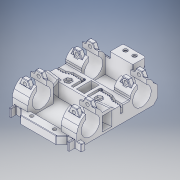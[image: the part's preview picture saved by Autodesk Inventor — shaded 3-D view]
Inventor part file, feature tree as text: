
AUTODESK INVENTOR PART (.ipt)
format: ipt  version: 2019.4 (Build 234330000, 330)  size: 2,265,088 bytes
history: native  units: mm
features: other x88, extrude x37, fillet x12, mirror x8, sketch x8, loft x5, projected_geometry x2, hole x1
ambient origin geometry x8: Origin, YZ Plane, XZ Plane, XY Plane, X Axis, Y Axis, Z Axis, Center Point
bodies: Solid1 (feature_tree)
feature tree (161):
  extrude  "Base"  Depth=67.2mm
  other  "Right Outside Vertical Plane"
  extrude  "Lower Right Rod Holder"  Depth=4.9mm
  fillet  "Bottom Round Fillet"  Radius=1.715mm
  other  "Bottom Rod Clasp Plane"
  other  "Bottom Rod Bottom Screw Hole Plane"
  other  "Bottom Clasp Hole Sketch"
  loft  "Bottom Right Clasp Loft"
  extrude  "Bottom Clasp Hole"  Depth=49.274mm
  other  "Bottom Right Clasp Mirror Plane"
  mirror  "Bottom Right Top Clasp"
  mirror  "Bottom Left Rod Assembly"
  other  "Bottom Middle Extrusion Plane"
  extrude  "Bottom Middle Extrusion"  Depth=4.2mm
  extrude  "Bottom Side Extrusions"  Depth=14.573499mm
  extrude  "Top Rod Extrusion"  Depth=30.281463mm
  other  "Bottom Right Inner Clasp Plane"
  other  "Bottom Left Inner Clasp Plane"
  extrude  "Top Rod Cutout"  Depth=10.0mm TaperAngle=0.0deg
  other  "Top Right Bottom Rod Clasp Plane"
  other  "Top Right Bottom Rod Clasp sketch"
  other  "Bottom Nut Plane"
  other  "Nut Holder Sketch"
  other  "Nut Hole"
  loft  "Bottom Top Right Clasp Loft"
  extrude  "Bottom Top Right Clasp Hole"  Depth=10.0mm
  other  "Top Right Clasp Mirror Plane"
  mirror  "Top Top Right Clasp Assembly"
  mirror  "Top Left Clasp Assembly"
  extrude  "Middle Extrusion"  Depth=10.0mm
  extrude  "Middle Extrusion Center Cutout"  Depth=10.0mm TaperAngle=0.0deg
  other  "Top GT2 Cable Plane"
  extrude  "GT2 Cable Cutout"  Depth=10.0mm
  extrude  "Nut Cutout"  Depth=10.0mm
  other  "Nut Screw Cutout Plane"
  extrude  "Nut Screw Cutout"  TaperAngle=0.0deg  [1 undecoded]
  other  "Right Outside Drag / Cable Plane"
  extrude  "Track Platform"  [1 undecoded]
  extrude  "Sensor Container"  TaperAngle=0.0deg  [1 undecoded]
  extrude  "Insert Holes Cutout"  Depth=10.0mm
  extrude  "Lower Rod Support Extrusion"  Depth=10.0mm TaperAngle=0.0deg
  other  "Right Outside Vertical Plane 2"
  other  "Outside Triangle Bottom Clasp Support Sketch"
  other  "Inside Bottom Clasp Support Plane"
  loft  "Lower Rod Support Loft"
  fillet  "GT2 Bottom Round Fillet (4)"  [1 undecoded]
  mirror  "Lower Rod Support Mirrored"
  fillet  "Bottom Trim Fillets (.2)"  Radius=4.76mm
  fillet  "Bottom Trim Fillets (1)"  Radius=4.76mm
  other  "First Top Track Cut Plane"
  extrude  "First Top Track Cut"  Depth=10.0mm
  extrude  "First Inner Bottom Track Cut Extrusion"  Depth=10.0mm
  other  "First Inner Bottom Angled Track Cut Plane"
  extrude  "First Outer Bottom Track Cut Extrusion"  Depth=10.0mm
  other  "Second Inner Bottom Plane"
  other  "Third Inner Bottom Plane"
  other  "Fourth Inner Bottom Plane"
  other  "Fifth Inner Bottom Plane"
  other  "Sixth Inner Bottom Plane"
  other  "Seventh Inner Bottom Plane"
  other  "First Inner Bottom Angle Plane"
  other  "Second Inner Bottom Angle Plane"
  other  "Third Inner Bottom Angle Plane"
  other  "Fourth Inner Bottom Angle Plane"
  other  "Fifth Inner Bottom Angle Plane"
  other  "Sixth Inner Bottom Angle Plane"
  other  "Eight Inner Bottom Plane"
  other  "Ninth Inner Bottom Plane"
  other  "Tenth Inner Bottom Plane"
  other  "Eleventh Inner Bottom Plane"
  other  "Twelth Inner Bottom Plane"
  other  "Thirteenth Inner Bottom Plane"
  other  "Fourteenth Inner Bottom Plane"
  extrude  "Second Outer Bottom Extrusion"  Depth=10.0mm
  extrude  "Third Outer Bottom Extrusion"  Depth=10.0mm TaperAngle=0.0deg
  extrude  "Fourth Outer Bottom Extrusion"  [1 undecoded]
  other  "Inbetween Fourth Angle Plane"
  extrude  "First Inner Bottom Angle Extrusion"  [1 undecoded]
  other  "First Top Angle Plane"
  other  "First Bend Upper Angle Sketch"
  other  "Second Top Angle Plane"
  extrude  "Top Angle Extrusion"  Depth=10.0mm
  other  "Top Outside Border Plane"
  other  "Top Outside Border Sketch"
  other  "Top Second Insider Border Plane"
  other  "Top Inside Border Sketch"
  other  "Top Insider Border Plane"
  other  "Top Second Insider Border Sketch"
  loft  "Top Inside Border Loft"
  other  "Inside Top Last Border Sketch"
  extrude  "First Bottom Outer Angled Extrusion"  TaperAngle=0.0deg  [1 undecoded]
  extrude  "Second Bottom Outer Angled Extrusion"  [1 undecoded]
  extrude  "Third Bottom Outer Angled Extrusion"  Depth=10.0mm
  extrude  "Fifth Bottom Outer Extrusion"  TaperAngle=0.0deg  [1 undecoded]
  extrude  "Sixth Bottom Outer Extrusion"  TaperAngle=0.0deg  [1 undecoded]
  extrude  "Seventh Bottom Outer Extrusion"  Depth=10.0mm TaperAngle=0.0deg
  extrude  "Eigth Bottom Outer Extrusion"  Depth=10.0mm
  other  "Second Inner Bottom Sketch"
  extrude  "Second Inner Bottom Track Cut Extrusion"  Depth=10.0mm
  loft  "Second Inner Bottom Track Loft"
  mirror  "Track Mirror"
  other  "Right Outside Vertical Plane 3"
  extrude  "Endstop Extrusion (4)"  Depth=10.0mm
  extrude  "Drag / Cable Extrusion (4.6)"  Depth=10.0mm TaperAngle=0.0deg
  hole  "Drag / Cable Holes"  [1 undecoded]
  other  "Vertical Middle Mirror Plane"
  other  "Left Nut Buttom Plane"
  other  "Left Nut Buttom Sketch"
  fillet  "Bottom Middle Trim Fillet (.4)"  Radius=13.0mm
  fillet  "Bottom Top Clasp Fillet (.8)"  Radius=2.2mm
  fillet  "Top Drag / Cable Fillet (1.6)"  Radius=7.85mm
  fillet  "Bottom Drag / Cable Fillet (.4)"  [1 undecoded]
  fillet  "Bottom  Top Wire Holder Fillet (1)"  Radius=6.4mm
  fillet  "Top Top Wire Holder Trim (.3)"  Radius=13.4mm
  fillet  "Top Round Fillet (2.4)"  Radius=1.86mm
  fillet  "Nut Trim Fillets (.4)"  Radius=1.8mm
  other  "Left Bottom Nut Cutout Plane"
  extrude  "Top Left Bottom Nut Cutout Extrusion"  TaperAngle=0.0deg  [1 undecoded]
  mirror  "Top Bottom Nut Cutout Mirror"
  other  "Top Bottom Left Nut Cutout Extended Plane"
  other  "Top Bottom Left Nut Cutout Sketch"
  other  "Top Bottom Left Nut Cutout Plane"
  extrude  "Top Bottom Left Nut Cutout Extrusion"  Depth=10.0mm
  mirror  "Top Bottom Right Nut Cutout Extrusion Mirrored"
  sketch  "Sketch2"  dims[d0=56.4mm d2=67.2mm]
  other  "Bottom Clasp"
  other  "Bottom Middle Sketch"
  other  "Bottom Side Sketch"
  other  "Top Rod Sketch"
  other  "Top Rod Cutout Sketch"
  other  "Middle Extrusion Sketch"
  sketch  "Sketch13"  dims[d3=1.848mm d4=4.9mm d5=1.715mm]
  other  "GT2 Cable Sketch"
  other  "Nut Sketch"
  other  "Nut Screw Cutout Sketch"
  sketch  "Sketch19"  dims[d6=1.848mm d7=4.9mm]
  other  "Bottom Insert Holes"
  sketch  "Sketch21"  dims[d8=1.715mm d9=49.274mm]
  other  "Inside Triangle Bottom Clasp Sketch"
  other  "First Top Track Cut Sketch"
  other  "First Inner Bottom Track Cut Sketch"
  other  "First Outer Bottom Track Cut Sketch"
  other  "Second Outer Bottom Sketch"
  other  "Third Outer Bottom Sketch"
  other  "Fourth Outer Bottom Sketch"
  other  "First Inner Bottom Angle Sketch"
  projected_geometry  "Projected Loop6"
  sketch  "Sketch48"  dims[d11=1.134464mm d13=4.2mm]
  other  "First Bottom Outer Angled Sketch"
  other  "Second Bottom Outer Angled Sketch"
  other  "Third Bottom Outer Angled Sketch"
  other  "Fifth Bottom Outer Sketch"
  other  "Sixth Bottom Outer Sketch"
  other  "Seventh Bottom Outer Sketch"
  other  "Eigth Bottom Outer Sketch"
  sketch  "Sketch60"  dims[d15=7.0mm d16=14.573499mm]
  other  "Edges1"
  sketch  "Sketch61"  dims[d17=4.2mm d18=30.281463mm]
  other  "Drag / Cable Sketch"
  projected_geometry  "Projected Loop7"
  sketch  "Sketch63"  dims[d19=7.0mm d20=2.052mm d21=0.0mm d22=0.0mm d23=16.2mm d24=10.6mm d28=21.816616mm d29=13.6mm d30=0.0mm d31=9.75mm d32=8.4mm d33=0.0mm d35=-3.5mm d37=0.0mm d38=90.0deg d39=0.0mm d40=90.0deg d41=3.0mm d42=13.6mm d43=0.0mm d44=4.2mm d45=0.0mm d46=4.76mm d47=0.0mm d48=4.76mm d49=0.0mm d50=16.2mm d51=10.6mm d53=8.4mm d54=5.43mm d55=7.15585mm d56=9.582mm d57=4.76mm d58=0.0mm d59=-14.0mm d60=-14.0mm d61=16.2mm d62=10.6mm d63=8.4mm d67=4.76mm d68=0.0mm d69=0.0mm d71=-3.5mm d72=3.0mm d73=0.0mm d74=90.0deg d75=0.0mm d76=90.0deg d77=4.76mm d78=0.0mm d79=4.2mm d80=15.95mm d84=11.496474mm d85=11.496474mm d86=12.2mm d87=0.0mm d88=7.0mm d89=13.0mm d90=2.2mm d91=7.85mm d92=0.0mm d93=0.0mm d96=6.4mm d97=0.0mm d98=13.4mm d99=1.86mm d100=1.8mm d101=0.0mm d102=0.0mm d103=3.0mm d104=3.0mm d105=1.8mm d106=0.0mm d107=10.0mm d108=7.0mm d112=20.0mm d113=0.0mm d126=20.0mm d127=0.0mm d128=3.0mm d129=10.0mm d132=1.611mm d135=20.0mm d136=0.0mm d137=2.658mm d138=0.0mm d139=0.0mm d140=3.6mm d141=0.0mm d142=90.0deg d143=0.0mm d144=90.0deg d145=4.0mm d146=0.4mm d147=1.0mm d148=33.088mm d149=14.8mm d150=14.8mm d151=4.136201mm d152=6.4mm d153=0.750008mm d154=2.4mm d155=13.962634mm d156=10.0mm d157=0.0mm d162=10.0mm d163=0.0mm d171=0.373mm d172=90.0deg d173=0.373mm d174=90.0deg d175=10.0mm d176=0.0mm d177=0.0mm d178=0.0mm d179=0.0mm d180=0.0mm d181=0.0mm d182=0.0mm d183=0.0mm d184=0.0mm d185=0.0mm d186=0.0mm d187=0.0mm d188=0.0mm d189=0.0mm d190=0.0mm d191=0.0mm d192=0.0mm d193=0.0mm d194=0.0mm d195=0.0mm d200=10.0mm d201=0.0mm d202=10.0mm d203=0.0mm d204=10.0mm d205=0.0mm d212=0.373mm d213=10.0mm d214=0.0mm d222=10.0mm d223=0.0mm d234=0.0mm d235=90.0deg d236=0.0mm d237=90.0deg d240=10.0mm d241=0.0mm d242=10.0mm d243=0.0mm d244=10.0mm d245=0.0mm d246=10.0mm d247=0.0mm d248=10.0mm d249=0.0mm d250=10.0mm d251=0.0mm d252=10.0mm d253=0.0mm d254=0.4mm d259=10.0mm d260=0.0mm d261=0.0mm d262=90.0deg d263=0.0mm d264=90.0deg d265=0.0mm d266=3.4mm d267=5.8mm d268=4.0mm d269=0.0mm d270=4.6mm d271=0.0mm d272=4.0mm d273=4.0mm d274=3.0mm d275=6.0mm d276=3.6mm d277=1.2mm d278=90.0deg d279=9.25mm d280=0.0mm d285=-28.2mm d287=2.0mm d288=3.175mm d291=0.4mm d292=0.8mm d293=1.6mm d294=0.4mm d295=1.0mm d296=0.3mm d297=2.4mm d298=0.4mm d299=10.0mm d300=0.0mm d301=0.8mm d302=3.175mm d303=10.0mm d304=0.0mm]
note: 13 required parameter values undecoded (feature->parameter linkage not recoverable at this tier; creation-order binding heuristic only, values carry confidence <= 0.55)
